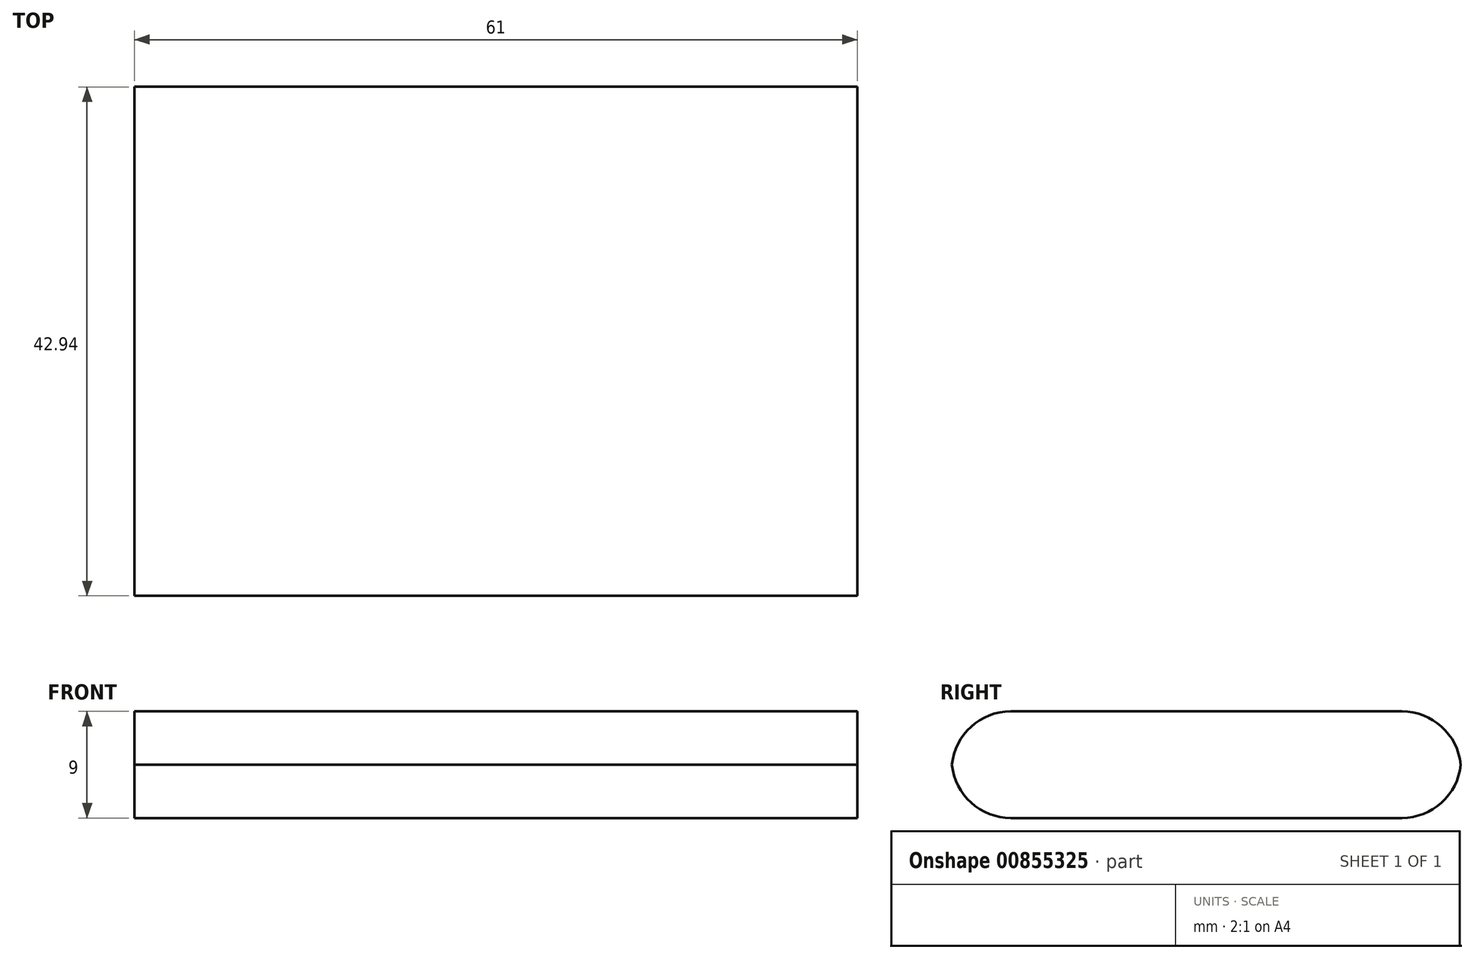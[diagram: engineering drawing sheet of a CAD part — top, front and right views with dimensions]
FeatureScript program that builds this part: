
annotation { "Feature Type Name" : "Feature", "Feature Type Description" : "" }
export const myFeature = defineFeature(function(context is Context, id is Id, definition is map)
    precondition{}
    {
        {
            var Q0;
            Q0=qCreatedBy(makeId("Top.planeOp"),FACE);
            var sketch = newSketch(context, id + "F0", { "sketchPlane" : qUnion([Q0])});
            skLineSegment(sketch, "E0.bottom", {"start": v(-30.5, 21.5) * mm, "end": v(30.5, 21.5) * mm});
            skLineSegment(sketch, "E0.top", {"start": v(-30.5, -21.5) * mm, "end": v(30.5, -21.5) * mm});
            skLineSegment(sketch, "E0.left", {"start": v(-30.5, 21.5) * mm, "end": v(-30.5, -21.5) * mm});
            skLineSegment(sketch, "E0.right", {"start": v(30.5, 21.5) * mm, "end": v(30.5, -21.5) * mm});
            skPoint(sketch, "E0.middle", {"position": v(0, 0) * mm});
            skSolve(sketch);
        }
        {
            var Q0;
            Q0 = qSketchRegion(id + "F0", true);
            extrude(context, id + "F1", {"entities" : qUnion([Q0]), "depth" : 9 * mm, "offsetDistance" : 25 * mm});
        }
        {
            var Q0;
            Q0=makeQuery(id+"F1.opExtrude","CAP_EDGE",EDGE,{"disambiguationData":[OSD([sQuery(id+"F0.wireOp",EDGE,"E0.bottom")])],"isStart":false});
            var Q1;
            Q1=makeQuery(id+"F1.opExtrude","CAP_EDGE",EDGE,{"disambiguationData":[OSD([sQuery(id+"F0.wireOp",EDGE,"E0.top")])],"isStart":false});
            var Q2;
            Q2=makeQuery(id+"F1.opExtrude","CAP_EDGE",EDGE,{"disambiguationData":[OSD([sQuery(id+"F0.wireOp",EDGE,"E0.top")])],"isStart":true});
            var Q3;
            Q3=makeQuery(id+"F1.opExtrude","CAP_EDGE",EDGE,{"disambiguationData":[OSD([sQuery(id+"F0.wireOp",EDGE,"E0.bottom")])],"isStart":true});
            fillet(context, id + "F2", {"entities" : qUnion([Q0, Q1, Q2, Q3]), "radius" : 5 * mm, "tangentPropagation" : true, "allowEdgeOverflow" : false});
        }
    });
